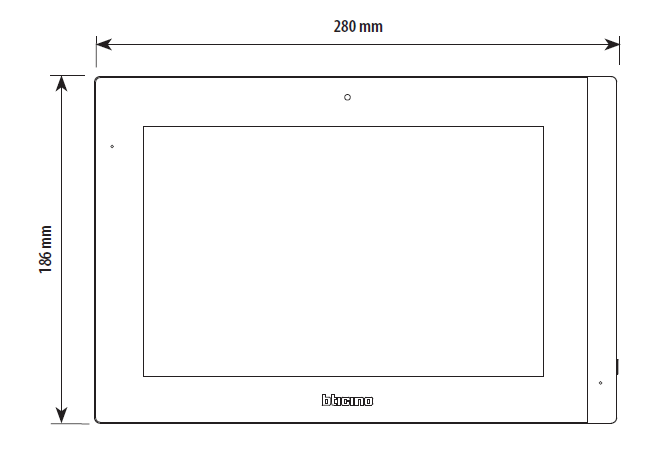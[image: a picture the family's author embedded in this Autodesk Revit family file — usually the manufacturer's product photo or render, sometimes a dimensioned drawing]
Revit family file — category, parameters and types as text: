
# Revit family: Legrand_Gestion_Numerique_Batiment_BMSIOT_Donnees
name_source: partatom
category: Dispositifs de données
units: mm (PartAtom-declared; Revit-internal decimal feet)

## family parameters
Conserver l'orientation des annotations = Non
Cote de connecteur circulaire = Utiliser le diamètre
Couper avec des vides une fois chargée = Non
Hôte = Face
Numéro OmniClass = 23.85.50.17
Partagée = Non
Repere pour localisation dans la piece = Non
Titre OmniClass = Communication and Data Processing Equipment
Type d'élément = Normal

## types (1)
- Area Manager
    Bluetooth BLE = Oui
    Classe ETIM = EC001099-interface de système/média-gateway de système bus
    Classe POE = Class1
    Code EAN = 3414972772341
    Conditions Générale d'Utilisation = https://export.legrand.com
    Couleur = Blanc
    Description = Contrôleur GTB Area Manager pour la gestion des bâtiment et de l'efficacité énergétique
    Distance paramétrable = Oui
    Désignation produit = AREA MANAGER
    Elévation par défaut = 1219.2 mm  [stored 4 ft]
    Fabricant = LEGRAND
    Hauteur = 28.7 mm  [stored 0.0941601 ft]
    IK = 10
    IP = 20
    Largeur = 116 mm  [stored 0.380577 ft]
    MATERIAU = LEGRAND_PVC_BLANC
    Matière = Plastique
    Modèle = BMS IOT
    Norme POE = 802.3af
    Poids = 211 g
    Profondeur = 106 mm  [stored 0.347769 ft]
    Protocole de Communication = TCP/UDP
    Référence / Modèle = 048584
    Temperature d'utilisation MIN-MAX = 0°C - +40°C
    URL = https://www.legrand.fr
    Wifi = Oui
    Zigbee = Oui

note: [stored X ft] marks values corroborated as IEEE doubles in the binary element streams (Revit-internal decimal feet)
